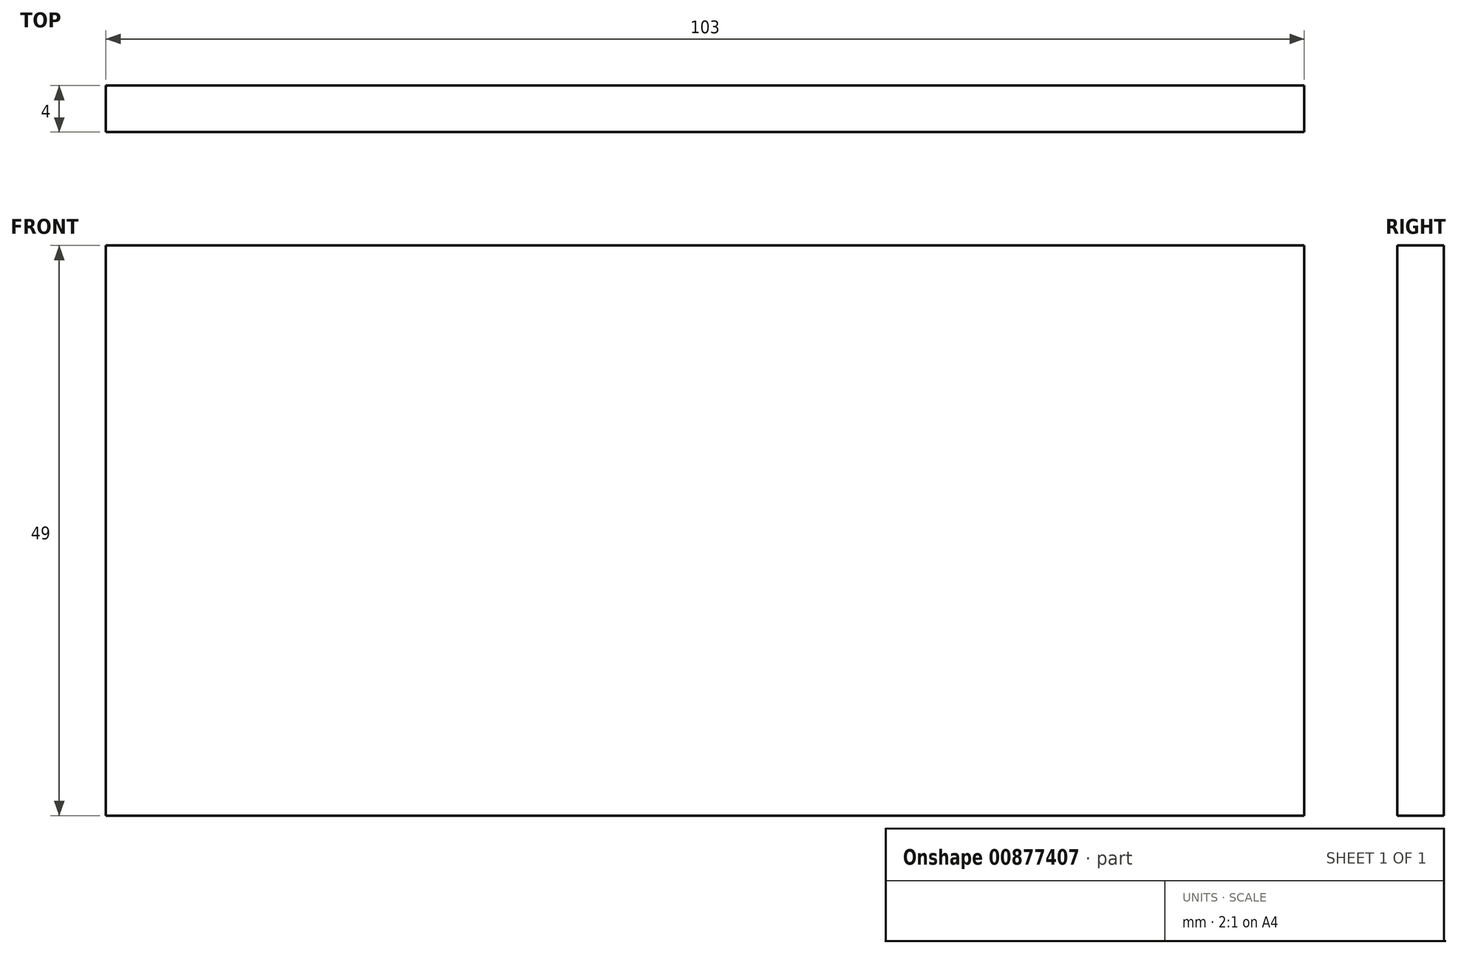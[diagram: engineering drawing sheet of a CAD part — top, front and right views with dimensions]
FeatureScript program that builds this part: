
annotation { "Feature Type Name" : "Feature", "Feature Type Description" : "" }
export const myFeature = defineFeature(function(context is Context, id is Id, definition is map)
    precondition{}
    {
        {
            var Q0;
            Q0=qCreatedBy(makeId("Top.planeOp"),FACE);
            var sketch = newSketch(context, id + "F0", { "sketchPlane" : qUnion([Q0])});
            skLineSegment(sketch, "E0.bottom", {"start": v(51.5, -2) * mm, "end": v(-51.5, -2) * mm});
            skLineSegment(sketch, "E0.top", {"start": v(51.5, 2) * mm, "end": v(-51.5, 2) * mm});
            skLineSegment(sketch, "E0.left", {"start": v(51.5, -2) * mm, "end": v(51.5, 2) * mm});
            skLineSegment(sketch, "E0.right", {"start": v(-51.5, -2) * mm, "end": v(-51.5, 2) * mm});
            skPoint(sketch, "E0.middle", {"position": v(0, 0) * mm});
            skSolve(sketch);
        }
        {
            var Q0;
            Q0=makeQuery(id+"F0.imprint","IMPRINT",FACE,{"disambiguationData":[TD([[makeQuery(id+"F0.imprint","IMPRINT",EDGE,{"derivedFrom":sQuery(id+"F0.wireOp",EDGE,"E0.bottom")}),-1.0]])]});
            extrude(context, id + "F1", {"entities" : qUnion([Q0]), "depth" : 49 * mm, "offsetDistance" : 25.4 * mm});
        }
    });
